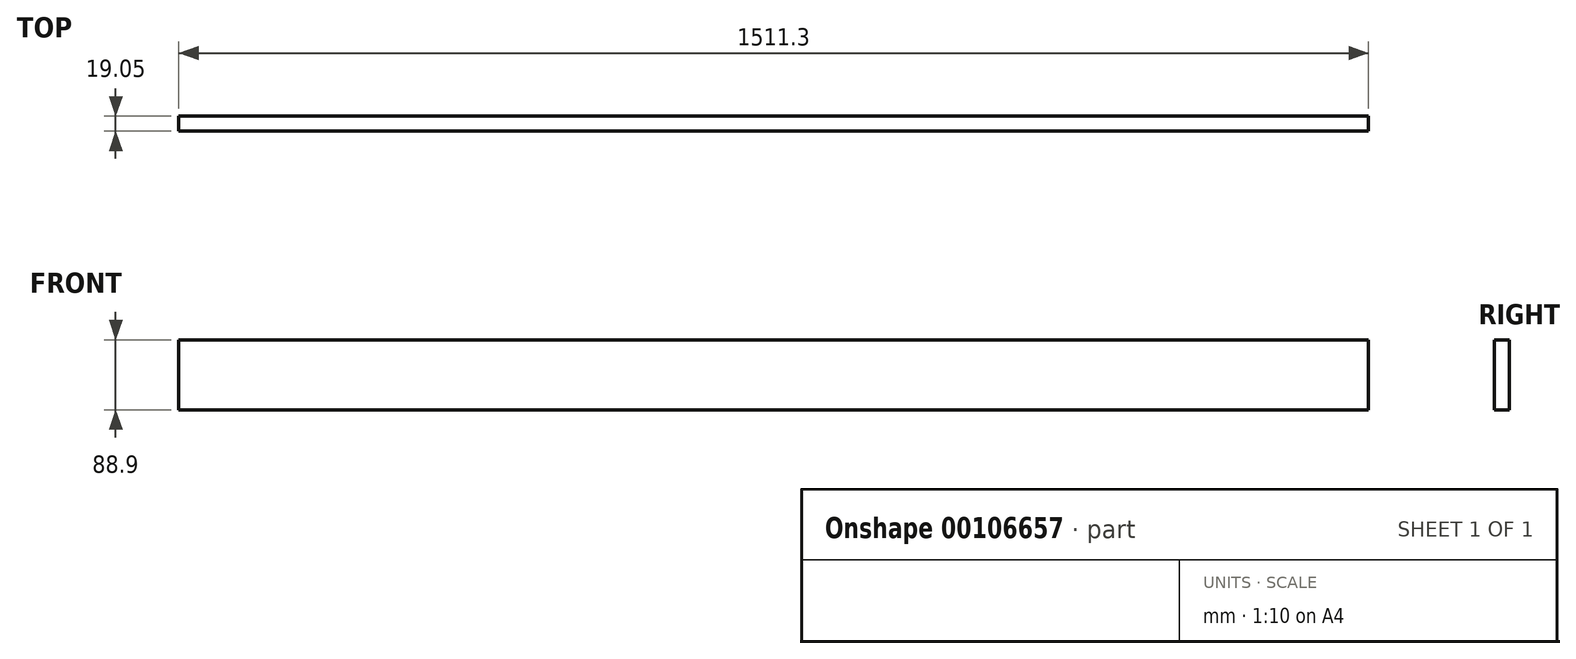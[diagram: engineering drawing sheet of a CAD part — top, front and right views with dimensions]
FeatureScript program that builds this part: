
annotation { "Feature Type Name" : "Feature", "Feature Type Description" : "" }
export const myFeature = defineFeature(function(context is Context, id is Id, definition is map)
    precondition{}
    {
        {
            var Q0;
            Q0=qCreatedBy(makeId("Front.planeOp"),FACE);
            var sketch = newSketch(context, id + "F0", { "sketchPlane" : qUnion([Q0])});
            skLineSegment(sketch, "E0.bottom", {"start": v(0, 0) * mm, "end": v(1511.3, 0) * mm});
            skLineSegment(sketch, "E0.top", {"start": v(0, 88.9) * mm, "end": v(1511.3, 88.9) * mm});
            skLineSegment(sketch, "E0.left", {"start": v(0, 0) * mm, "end": v(0, 88.9) * mm});
            skLineSegment(sketch, "E0.right", {"start": v(1511.3, 0) * mm, "end": v(1511.3, 88.9) * mm});
            skSolve(sketch);
        }
        {
            var Q0;
            Q0=makeQuery(id+"F0.imprint","IMPRINT",FACE,{"disambiguationData":[TD([[makeQuery(id+"F0.imprint","IMPRINT",EDGE,{"derivedFrom":sQuery(id+"F0.wireOp",EDGE,"E0.bottom")}),1.0]])]});
            extrude(context, id + "F1", {"entities" : qUnion([Q0]), "depth" : 19.05 * mm});
        }
    });
